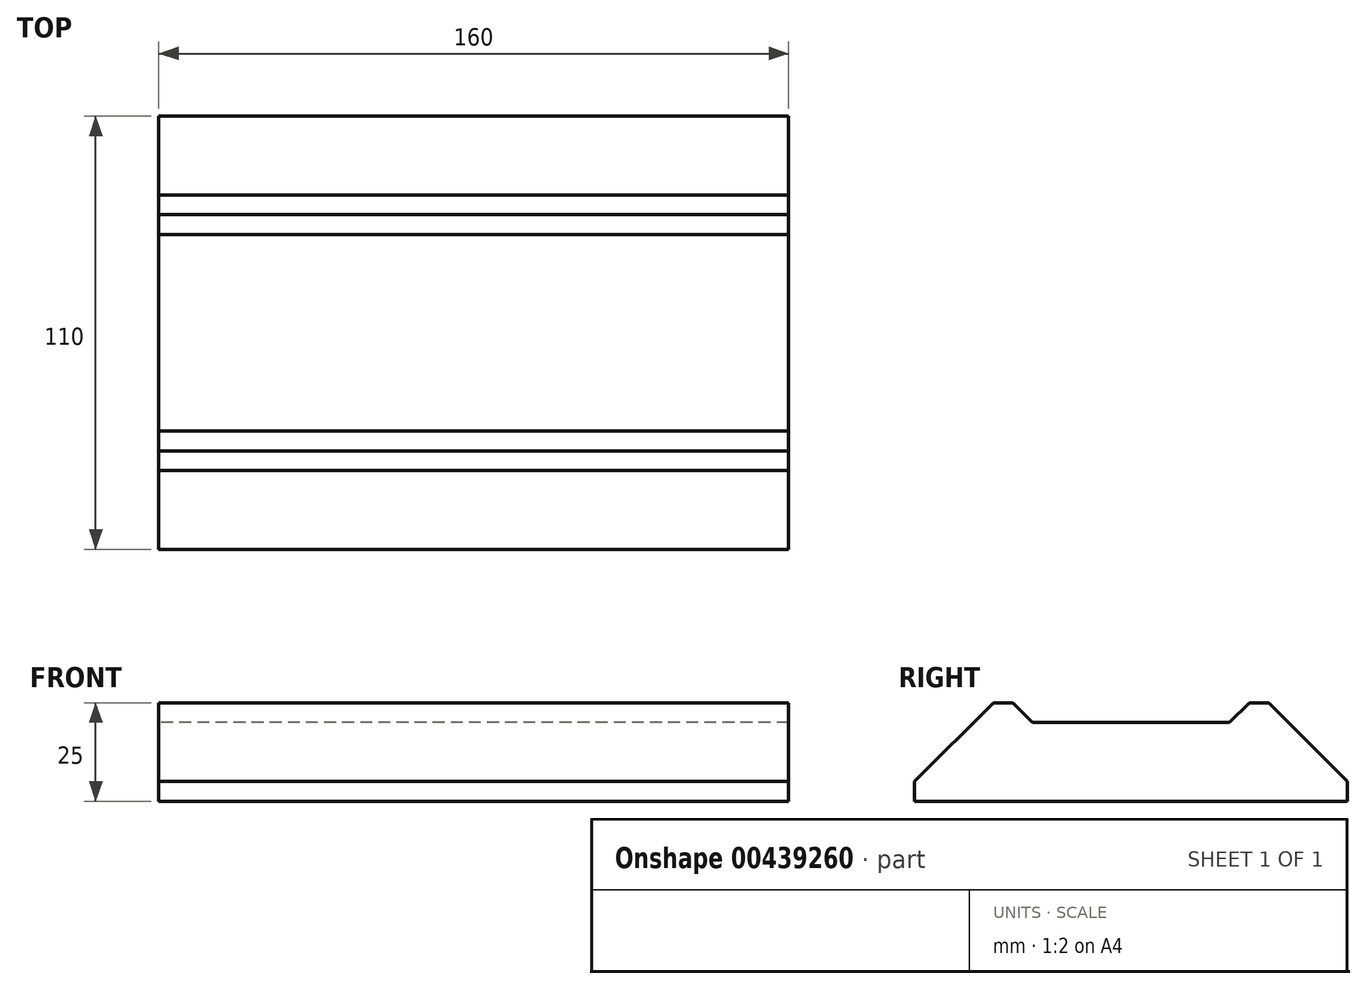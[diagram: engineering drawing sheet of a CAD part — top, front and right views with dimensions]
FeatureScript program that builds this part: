
annotation { "Feature Type Name" : "Feature", "Feature Type Description" : "" }
export const myFeature = defineFeature(function(context is Context, id is Id, definition is map)
    precondition{}
    {
        {
            var Q0;
            Q0=qCreatedBy(makeId("Top.planeOp"),FACE);
            var sketch = newSketch(context, id + "F0", { "sketchPlane" : qUnion([Q0])});
            skLineSegment(sketch, "E0.bottom", {"start": v(-77.48, 9.11) * mm, "end": v(82.52, 9.11) * mm});
            skLineSegment(sketch, "E0.top", {"start": v(-77.48, -50.89) * mm, "end": v(82.52, -50.89) * mm});
            skLineSegment(sketch, "E0.left", {"start": v(-77.48, 9.11) * mm, "end": v(-77.48, -50.89) * mm});
            skLineSegment(sketch, "E0.right", {"start": v(82.52, 9.11) * mm, "end": v(82.52, -50.89) * mm});
            skLineSegment(sketch, "E1.top", {"start": v(-77.48, 4.11) * mm, "end": v(82.52, 4.11) * mm});
            skLineSegment(sketch, "E1.left", {"start": v(-77.48, 9.11) * mm, "end": v(-77.48, 4.11) * mm});
            skLineSegment(sketch, "E1.right", {"start": v(82.52, 9.11) * mm, "end": v(82.52, 4.11) * mm});
            skLineSegment(sketch, "E2.top", {"start": v(-77.48, -45.89) * mm, "end": v(82.52, -45.89) * mm});
            skLineSegment(sketch, "E2.left", {"start": v(-77.48, -50.89) * mm, "end": v(-77.48, -45.89) * mm});
            skLineSegment(sketch, "E2.right", {"start": v(82.52, -50.89) * mm, "end": v(82.52, -45.89) * mm});
            skSolve(sketch);
        }
        {
            var Q0;
            Q0=makeQuery(id+"F0.imprint","IMPRINT",FACE,{"disambiguationData":[TD([[makeQuery(id+"F0.imprint","IMPRINT",EDGE,{"derivedFrom":sQuery(id+"F0.wireOp",EDGE,"E0.bottom")}),-1.0]])]});
            var Q1;
            Q1=makeQuery(id+"F0.imprint","IMPRINT",FACE,{"disambiguationData":[TD([[makeQuery(id+"F0.imprint","IMPRINT",EDGE,{"derivedFrom":sQuery(id+"F0.wireOp",EDGE,"E0.top")}),1.0]])]});
            extrude(context, id + "F1", {"entities" : qUnion([Q0, Q1]), "depth" : 25 * mm});
        }
        {
            var Q0;
            Q0=makeQuery(id+"F0.imprint","IMPRINT",FACE,{"disambiguationData":[TD([[makeQuery(id+"F0.imprint","IMPRINT",EDGE,{"derivedFrom":sQuery(id+"F0.wireOp",EDGE,"E0.left")}),1.0]])]});
            extrude(context, id + "F2", {"entities" : qUnion([Q0]), "depth" : 20 * mm});
        }
        {
            var Q0;
            Q0=makeQuery(id+"F1.opExtrude","CAP_EDGE",EDGE,{"disambiguationData":[OSD([sQuery(id+"F0.wireOp",EDGE,"E1.top")])],"isStart":false});
            var Q1;
            Q1=makeQuery(id+"F1.opExtrude","CAP_EDGE",EDGE,{"disambiguationData":[OSD([sQuery(id+"F0.wireOp",EDGE,"E2.top")])],"isStart":false});
            chamfer(context, id + "F3", {"entities" : qUnion([Q0, Q1]), "width" : 5 * mm, "tangentPropagation" : true});
        }
        {
            var Q0;
            Q0=makeQuery(id+"F1.opExtrude","SWEPT_FACE",FACE,{"disambiguationData":[OSD([sQuery(id+"F0.wireOp",EDGE,"E0.bottom")])]});
            extrude(context, id + "F4", {"entities" : qUnion([Q0]), "operationType" : NewBodyOperationType.ADD, "depth" : 25 * mm});
        }
        {
            var Q0;
            Q0=makeQuery(id+"F1.opExtrude","SWEPT_FACE",FACE,{"disambiguationData":[OSD([sQuery(id+"F0.wireOp",EDGE,"E0.top")])]});
            extrude(context, id + "F5", {"entities" : qUnion([Q0]), "operationType" : NewBodyOperationType.ADD, "depth" : 25 * mm});
        }
        {
            var Q0;
            Q0=makeQuery(id+"F4.opExtrude","CAP_EDGE",EDGE,{"disambiguationData":[OSD([sQuery(id+"F0.wireOp",EDGE,"E0.bottom"),sQuery(id+"F0.wireOp",EDGE,"E1.top")])],"isStart":false});
            var Q1;
            Q1=makeQuery(id+"F5.opExtrude","CAP_EDGE",EDGE,{"disambiguationData":[OSD([sQuery(id+"F0.wireOp",EDGE,"E0.top"),sQuery(id+"F0.wireOp",EDGE,"E2.top")])],"isStart":false});
            chamfer(context, id + "F6", {"entities" : qUnion([Q0, Q1]), "width" : 20 * mm, "tangentPropagation" : true});
        }
    });
